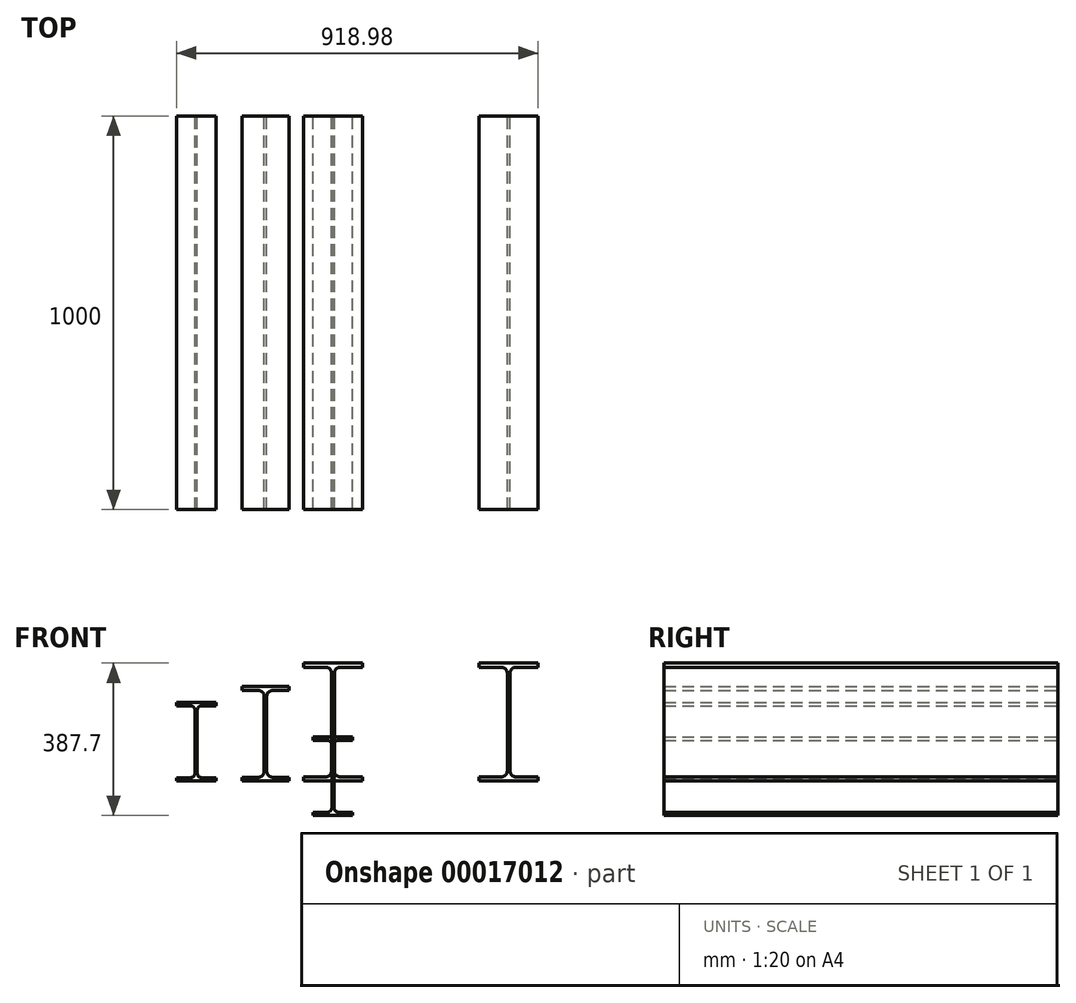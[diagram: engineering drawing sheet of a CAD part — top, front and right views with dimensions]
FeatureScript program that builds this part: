
annotation { "Feature Type Name" : "Feature", "Feature Type Description" : "" }
export const myFeature = defineFeature(function(context is Context, id is Id, definition is map)
    precondition{}
    {
        {
            var Q0;
            Q0=qCreatedBy(makeId("Front.planeOp"),FACE);
            var sketch = newSketch(context, id + "F0", { "sketchPlane" : qUnion([Q0])});
            skLineSegment(sketch, "E0", {"start": v(-75, 0) * mm, "end": v(75, 0) * mm});
            skLineSegment(sketch, "E1", {"start": v(75, 0) * mm, "end": v(75, 10.7) * mm});
            skLineSegment(sketch, "E2", {"start": v(75, 10.7) * mm, "end": v(18.55, 10.7) * mm});
            skLineSegment(sketch, "E3", {"start": v(3.55, 25.7) * mm, "end": v(3.55, 274.3) * mm});
            skLineSegment(sketch, "E4", {"start": v(18.55, 289.3) * mm, "end": v(75, 289.3) * mm});
            skLineSegment(sketch, "E5", {"start": v(75, 289.3) * mm, "end": v(75, 300) * mm});
            skLineSegment(sketch, "E6", {"start": v(75, 300) * mm, "end": v(-75, 300) * mm});
            skLineSegment(sketch, "E7", {"start": v(-75, 300) * mm, "end": v(-75, 289.3) * mm});
            skLineSegment(sketch, "E8", {"start": v(-75, 289.3) * mm, "end": v(-18.55, 289.3) * mm});
            skLineSegment(sketch, "E9", {"start": v(-3.55, 274.3) * mm, "end": v(-3.55, 25.7) * mm});
            skLineSegment(sketch, "E10", {"start": v(-18.55, 10.7) * mm, "end": v(-75, 10.7) * mm});
            skLineSegment(sketch, "E11", {"start": v(-75, 10.7) * mm, "end": v(-75, 0) * mm});
            skLineSegment(sketch, "E12", {"start": v(-3.55, 10.7) * mm, "end": v(3.55, 10.7) * mm, "construction": true});
            skPoint(sketch, "E13", {"position": v(0, 10.7) * mm});
            skPoint(sketch, "E14.visualSharp", {"position": v(3.55, 289.3) * mm});
            skArc(sketch, "E14.filletArc", {"start": v(18.55, 289.3) * mm, "mid": v(7.94, 284.9) * mm, "end": v(3.55, 274.3) * mm});
            skPoint(sketch, "E15.visualSharp", {"position": v(-3.55, 289.3) * mm});
            skArc(sketch, "E15.filletArc", {"start": v(-3.55, 274.3) * mm, "mid": v(-7.94, 284.9) * mm, "end": v(-18.55, 289.3) * mm});
            skPoint(sketch, "E16.visualSharp", {"position": v(-3.55, 10.7) * mm});
            skArc(sketch, "E16.filletArc", {"start": v(-18.55, 10.7) * mm, "mid": v(-7.94, 15.1) * mm, "end": v(-3.55, 25.7) * mm});
            skPoint(sketch, "E17.visualSharp", {"position": v(3.55, 10.7) * mm});
            skArc(sketch, "E17.filletArc", {"start": v(3.55, 25.7) * mm, "mid": v(7.94, 15.1) * mm, "end": v(18.55, 10.7) * mm});
            skSolve(sketch);
        }
        {
            var Q0;
            Q0=makeQuery(id+"F0.imprint","IMPRINT",FACE,{"disambiguationData":[TD([[makeQuery(id+"F0.imprint","IMPRINT",EDGE,{"derivedFrom":sQuery(id+"F0.wireOp",EDGE,"E0")}),1.0]])]});
            extrude(context, id + "F1", {"entities" : qUnion([Q0]), "depth" : 1000 * mm});
        }
        {
            var Q0;
            Q0=qCreatedBy(makeId("Front.planeOp"),FACE);
            var sketch = newSketch(context, id + "F2", { "sketchPlane" : qUnion([Q0])});
            skLineSegment(sketch, "E18", {"start": v(-231.3, 0) * mm, "end": v(-111.3, 0) * mm});
            skLineSegment(sketch, "E19", {"start": v(-111.3, 0) * mm, "end": v(-111.3, 9.8) * mm});
            skLineSegment(sketch, "E20", {"start": v(-111.3, 9.8) * mm, "end": v(-153.2, 9.8) * mm});
            skLineSegment(sketch, "E21", {"start": v(-168.2, 24.8) * mm, "end": v(-168.2, 215.2) * mm});
            skLineSegment(sketch, "E22", {"start": v(-153.2, 230.2) * mm, "end": v(-111.3, 230.2) * mm});
            skLineSegment(sketch, "E23", {"start": v(-111.3, 230.2) * mm, "end": v(-111.3, 240) * mm});
            skLineSegment(sketch, "E24", {"start": v(-111.3, 240) * mm, "end": v(-231.3, 240) * mm});
            skLineSegment(sketch, "E25", {"start": v(-231.3, 240) * mm, "end": v(-231.3, 230.2) * mm});
            skLineSegment(sketch, "E26", {"start": v(-231.3, 230.2) * mm, "end": v(-189.4, 230.2) * mm});
            skLineSegment(sketch, "E27", {"start": v(-174.4, 215.2) * mm, "end": v(-174.4, 24.8) * mm});
            skLineSegment(sketch, "E28", {"start": v(-189.4, 9.8) * mm, "end": v(-231.3, 9.8) * mm});
            skLineSegment(sketch, "E29", {"start": v(-231.3, 9.8) * mm, "end": v(-231.3, 0) * mm});
            skLineSegment(sketch, "E30", {"start": v(-174.4, 9.8) * mm, "end": v(-168.2, 9.8) * mm, "construction": true});
            skPoint(sketch, "E31", {"position": v(-171.3, 9.8) * mm});
            skPoint(sketch, "E32.visualSharp", {"position": v(-168.2, 230.2) * mm});
            skArc(sketch, "E32.filletArc", {"start": v(-153.2, 230.2) * mm, "mid": v(-163.8, 225.8) * mm, "end": v(-168.2, 215.2) * mm});
            skPoint(sketch, "E33.visualSharp", {"position": v(-174.4, 230.2) * mm});
            skArc(sketch, "E33.filletArc", {"start": v(-174.4, 215.2) * mm, "mid": v(-178.8, 225.8) * mm, "end": v(-189.4, 230.2) * mm});
            skPoint(sketch, "E34.visualSharp", {"position": v(-174.4, 9.8) * mm});
            skArc(sketch, "E34.filletArc", {"start": v(-189.4, 9.8) * mm, "mid": v(-178.8, 14.2) * mm, "end": v(-174.4, 24.8) * mm});
            skPoint(sketch, "E35.visualSharp", {"position": v(-168.2, 9.8) * mm});
            skArc(sketch, "E35.filletArc", {"start": v(-168.2, 24.8) * mm, "mid": v(-163.8, 14.2) * mm, "end": v(-153.2, 9.8) * mm});
            skPoint(sketch, "E36", {"position": v(-171.3, 0) * mm});
            skSolve(sketch);
        }
        {
            var Q0;
            Q0=makeQuery(id+"F2.imprint","IMPRINT",FACE,{"disambiguationData":[TD([[makeQuery(id+"F2.imprint","IMPRINT",EDGE,{"derivedFrom":sQuery(id+"F2.wireOp",EDGE,"E18")}),1.0]])]});
            extrude(context, id + "F3", {"entities" : qUnion([Q0]), "depth" : 1000 * mm});
        }
        {
            var Q0;
            Q0=qCreatedBy(makeId("Front.planeOp"),FACE);
            var sketch = newSketch(context, id + "F4", { "sketchPlane" : qUnion([Q0])});
            skLineSegment(sketch, "E37", {"start": v(-397.54, 0) * mm, "end": v(-297.54, 0) * mm});
            skLineSegment(sketch, "E38", {"start": v(-297.54, 0) * mm, "end": v(-297.54, 8.5) * mm});
            skLineSegment(sketch, "E39", {"start": v(-297.54, 8.5) * mm, "end": v(-332.74, 8.5) * mm});
            skLineSegment(sketch, "E40", {"start": v(-344.74, 20.5) * mm, "end": v(-344.74, 179.5) * mm});
            skLineSegment(sketch, "E41", {"start": v(-332.74, 191.5) * mm, "end": v(-297.54, 191.5) * mm});
            skLineSegment(sketch, "E42", {"start": v(-297.54, 191.5) * mm, "end": v(-297.54, 200) * mm});
            skLineSegment(sketch, "E43", {"start": v(-297.54, 200) * mm, "end": v(-397.54, 200) * mm});
            skLineSegment(sketch, "E44", {"start": v(-397.54, 200) * mm, "end": v(-397.54, 191.5) * mm});
            skLineSegment(sketch, "E45", {"start": v(-397.54, 191.5) * mm, "end": v(-362.34, 191.5) * mm});
            skLineSegment(sketch, "E46", {"start": v(-350.34, 179.5) * mm, "end": v(-350.34, 20.5) * mm});
            skLineSegment(sketch, "E47", {"start": v(-362.34, 8.5) * mm, "end": v(-397.54, 8.5) * mm});
            skLineSegment(sketch, "E48", {"start": v(-397.54, 8.5) * mm, "end": v(-397.54, 0) * mm});
            skLineSegment(sketch, "E49", {"start": v(-350.34, 8.5) * mm, "end": v(-344.74, 8.5) * mm, "construction": true});
            skPoint(sketch, "E50", {"position": v(-347.54, 8.5) * mm});
            skPoint(sketch, "E51.visualSharp", {"position": v(-344.74, 191.5) * mm});
            skArc(sketch, "E51.filletArc", {"start": v(-332.74, 191.5) * mm, "mid": v(-341.23, 187.99) * mm, "end": v(-344.74, 179.5) * mm});
            skPoint(sketch, "E52.visualSharp", {"position": v(-350.34, 191.5) * mm});
            skArc(sketch, "E52.filletArc", {"start": v(-350.34, 179.5) * mm, "mid": v(-353.86, 187.99) * mm, "end": v(-362.34, 191.5) * mm});
            skPoint(sketch, "E53.visualSharp", {"position": v(-350.34, 8.5) * mm});
            skArc(sketch, "E53.filletArc", {"start": v(-362.34, 8.5) * mm, "mid": v(-353.86, 12.01) * mm, "end": v(-350.34, 20.5) * mm});
            skPoint(sketch, "E54.visualSharp", {"position": v(-344.74, 8.5) * mm});
            skArc(sketch, "E54.filletArc", {"start": v(-344.74, 20.5) * mm, "mid": v(-341.23, 12.01) * mm, "end": v(-332.74, 8.5) * mm});
            skPoint(sketch, "E55", {"position": v(-347.54, 0) * mm});
            skLineSegment(sketch, "E56", {"start": v(-50, -87.7) * mm, "end": v(50, -87.7) * mm});
            skLineSegment(sketch, "E57", {"start": v(50, -87.7) * mm, "end": v(50, -79.2) * mm});
            skLineSegment(sketch, "E58", {"start": v(50, -79.2) * mm, "end": v(14.8, -79.2) * mm});
            skLineSegment(sketch, "E59", {"start": v(2.8, -67.2) * mm, "end": v(2.8, 91.8) * mm});
            skLineSegment(sketch, "E60", {"start": v(14.8, 103.8) * mm, "end": v(50, 103.8) * mm});
            skLineSegment(sketch, "E61", {"start": v(50, 103.8) * mm, "end": v(50, 112.3) * mm});
            skLineSegment(sketch, "E62", {"start": v(50, 112.3) * mm, "end": v(-50, 112.3) * mm});
            skLineSegment(sketch, "E63", {"start": v(-50, 112.3) * mm, "end": v(-50, 103.8) * mm});
            skLineSegment(sketch, "E64", {"start": v(-50, 103.8) * mm, "end": v(-14.8, 103.8) * mm});
            skLineSegment(sketch, "E65", {"start": v(-2.8, 91.8) * mm, "end": v(-2.8, -67.2) * mm});
            skLineSegment(sketch, "E66", {"start": v(-14.8, -79.2) * mm, "end": v(-50, -79.2) * mm});
            skLineSegment(sketch, "E67", {"start": v(-50, -79.2) * mm, "end": v(-50, -87.7) * mm});
            skLineSegment(sketch, "E68", {"start": v(-2.8, -79.2) * mm, "end": v(2.8, -79.2) * mm, "construction": true});
            skPoint(sketch, "E69", {"position": v(0, -79.2) * mm});
            skPoint(sketch, "E70.visualSharp", {"position": v(2.8, 103.8) * mm});
            skArc(sketch, "E70.filletArc", {"start": v(14.8, 103.8) * mm, "mid": v(6.31, 100.29) * mm, "end": v(2.8, 91.8) * mm});
            skPoint(sketch, "E71.visualSharp", {"position": v(-2.8, 103.8) * mm});
            skArc(sketch, "E71.filletArc", {"start": v(-2.8, 91.8) * mm, "mid": v(-6.31, 100.29) * mm, "end": v(-14.8, 103.8) * mm});
            skPoint(sketch, "E72.visualSharp", {"position": v(-2.8, -79.2) * mm});
            skArc(sketch, "E72.filletArc", {"start": v(-14.8, -79.2) * mm, "mid": v(-6.31, -75.68) * mm, "end": v(-2.8, -67.2) * mm});
            skPoint(sketch, "E73.visualSharp", {"position": v(2.8, -79.2) * mm});
            skArc(sketch, "E73.filletArc", {"start": v(2.8, -67.2) * mm, "mid": v(6.31, -75.68) * mm, "end": v(14.8, -79.2) * mm});
            skPoint(sketch, "E74", {"position": v(0, -87.7) * mm});
            skSolve(sketch);
        }
        {
            var Q0;
            Q0 = qSketchRegion(id + "F4", true);
            extrude(context, id + "F5", {"entities" : qUnion([Q0]), "depth" : 1000 * mm});
        }
        {
            var Q0;
            Q0=makeQuery(id+"F1.opExtrude","SWEPT_BODY",BODY,{"disambiguationData":[OSD([sQuery(id+"F0.wireOp",EDGE,"E0"),sQuery(id+"F0.wireOp",EDGE,"E1"),sQuery(id+"F0.wireOp",EDGE,"E2"),sQuery(id+"F0.wireOp",EDGE,"E3"),sQuery(id+"F0.wireOp",EDGE,"E4"),sQuery(id+"F0.wireOp",EDGE,"E5"),sQuery(id+"F0.wireOp",EDGE,"E6"),sQuery(id+"F0.wireOp",EDGE,"E7"),sQuery(id+"F0.wireOp",EDGE,"E8"),sQuery(id+"F0.wireOp",EDGE,"E9"),sQuery(id+"F0.wireOp",EDGE,"E10"),sQuery(id+"F0.wireOp",EDGE,"E11"),sQuery(id+"F0.wireOp",EDGE,"E14.filletArc"),sQuery(id+"F0.wireOp",EDGE,"E15.filletArc"),sQuery(id+"F0.wireOp",EDGE,"E16.filletArc"),sQuery(id+"F0.wireOp",EDGE,"E17.filletArc")])]});
            transform(context, id + "F6", {"entities" : qUnion([Q0]), "transformType" : TransformType.TRANSLATION_3D, "dx" : 446.44 * mm, "dy" : 0 * mm, "dz" : 0 * mm, "makeCopy" : true});
        }
    });
